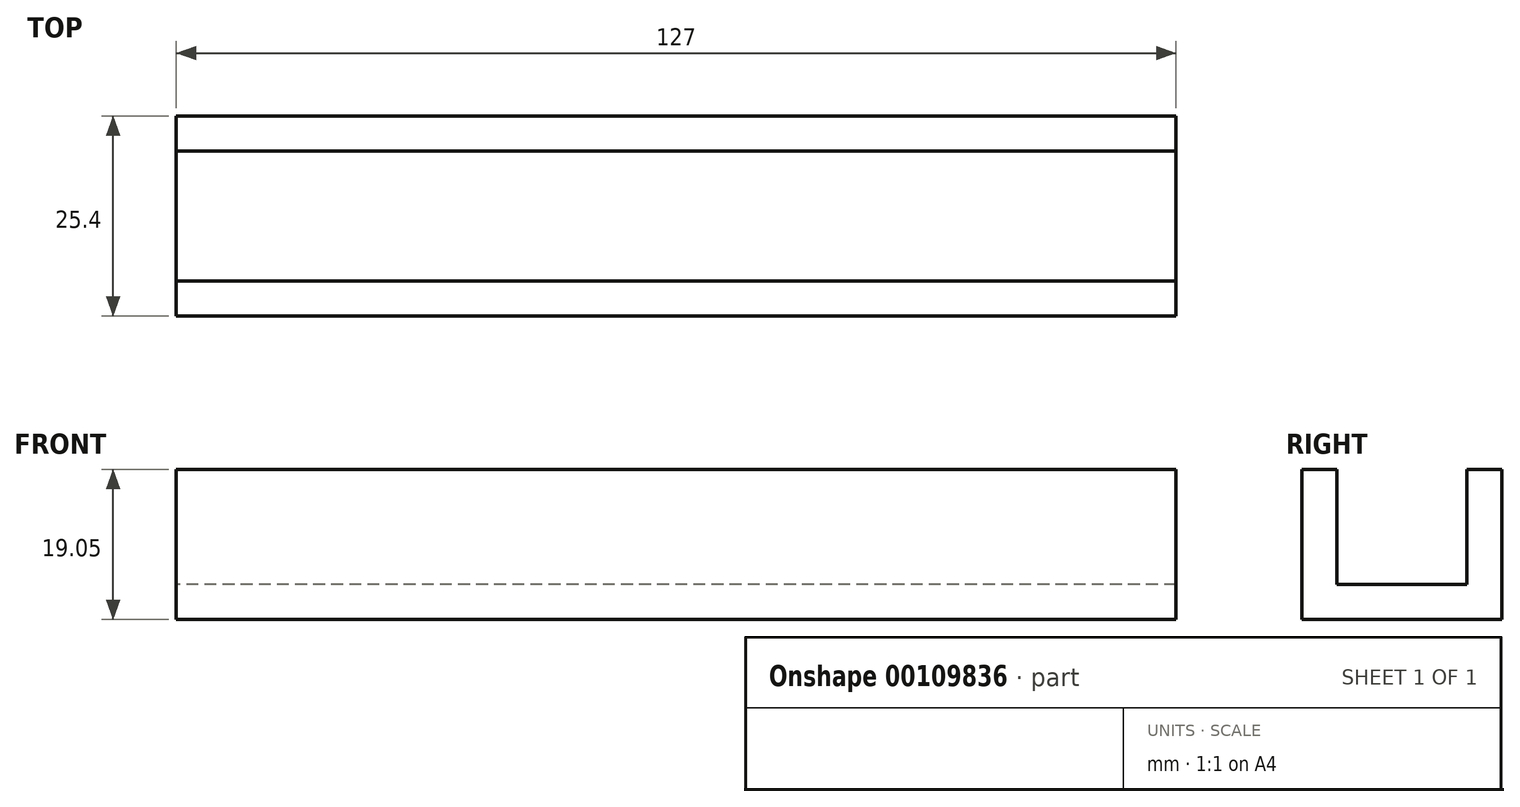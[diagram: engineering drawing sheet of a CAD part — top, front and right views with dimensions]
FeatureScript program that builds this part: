
annotation { "Feature Type Name" : "Feature", "Feature Type Description" : "" }
export const myFeature = defineFeature(function(context is Context, id is Id, definition is map)
    precondition{}
    {
        {
            var Q0;
            Q0=qCreatedBy(makeId("Right.planeOp"),FACE);
            var sketch = newSketch(context, id + "F0", { "sketchPlane" : qUnion([Q0])});
            skLineSegment(sketch, "E0", {"start": v(0, 0) * mm, "end": v(-12.7, 0) * mm});
            skLineSegment(sketch, "E1", {"start": v(-12.7, 0) * mm, "end": v(-12.7, 19.05) * mm});
            skLineSegment(sketch, "E2", {"start": v(-12.7, 19.05) * mm, "end": v(-8.26, 19.05) * mm});
            skLineSegment(sketch, "E3", {"start": v(-8.26, 19.05) * mm, "end": v(-8.26, 4.44) * mm});
            skLineSegment(sketch, "E4", {"start": v(-8.26, 4.44) * mm, "end": v(0, 4.45) * mm});
            skLineSegment(sketch, "E5.MirrorCS", {"start": v(12.7, 0) * mm, "end": v(12.7, 19.05) * mm});
            skLineSegment(sketch, "E6.MirrorCS", {"start": v(12.7, 19.05) * mm, "end": v(8.26, 19.05) * mm});
            skLineSegment(sketch, "E7.MirrorCS", {"start": v(8.26, 19.05) * mm, "end": v(8.26, 4.44) * mm});
            skLineSegment(sketch, "E8.MirrorCS", {"start": v(8.26, 4.44) * mm, "end": v(0, 4.45) * mm});
            skLineSegment(sketch, "E9.MirrorCS", {"start": v(0, 0) * mm, "end": v(12.7, 0) * mm});
            skSolve(sketch);
        }
        {
            var Q0;
            Q0=makeQuery(id+"F0.imprint","IMPRINT",FACE,{"disambiguationData":[TD([[makeQuery(id+"F0.imprint","IMPRINT",EDGE,{"derivedFrom":sQuery(id+"F0.wireOp",EDGE,"E0")}),-1.0]])]});
            extrude(context, id + "F1", {"entities" : qUnion([Q0]), "endBound" : BoundingType.SYMMETRIC, "depth" : 127 * mm});
        }
    });
